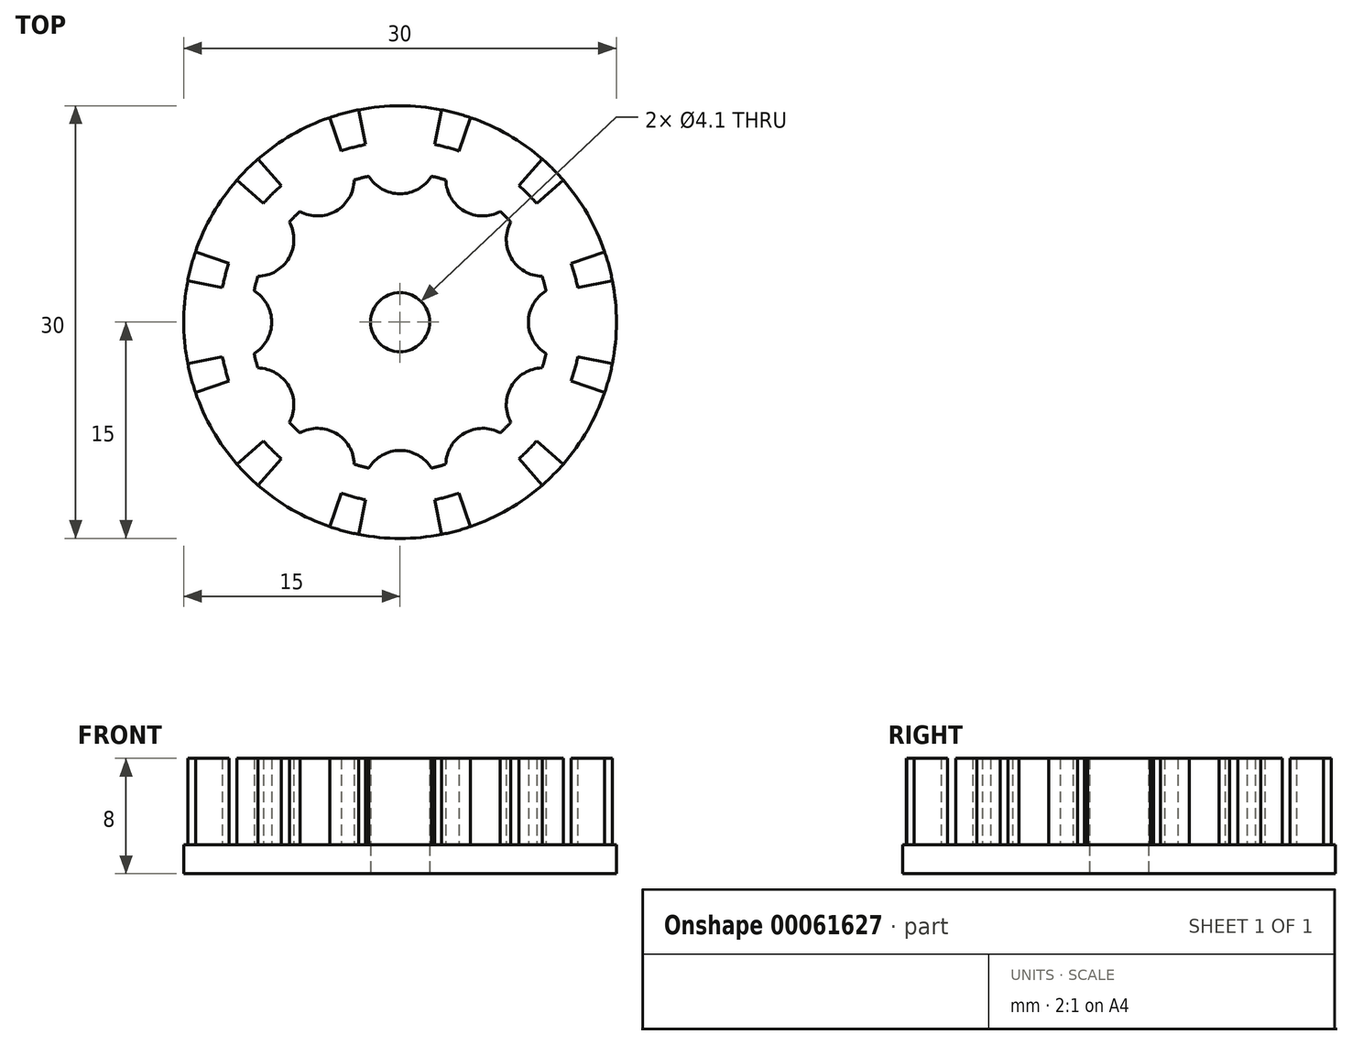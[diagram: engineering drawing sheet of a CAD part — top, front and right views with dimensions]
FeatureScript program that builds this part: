
annotation { "Feature Type Name" : "Feature", "Feature Type Description" : "" }
export const myFeature = defineFeature(function(context is Context, id is Id, definition is map)
    precondition{}
    {
        {
            var Q0;
            Q0=qCreatedBy(makeId("Top.planeOp"),FACE);
            var sketch = newSketch(context, id + "F0", { "sketchPlane" : qUnion([Q0])});
            skCircle(sketch, "E0", {"center": v(0, 0) * mm, "radius": 15 * mm});
            skArc(sketch, "E1.2.0", {"start": v(-9.85, 3.18) * mm, "mid": v(-7.7, 4.45) * mm, "end": v(-7.68, 6.94) * mm});
            skArc(sketch, "E2", {"start": v(-9.85, 3.18) * mm, "mid": v(-10, 2.68) * mm, "end": v(-10.12, 2.18) * mm});
            skArc(sketch, "E3", {"start": v(-11.87, 4.08) * mm, "mid": v(-12.12, 3.25) * mm, "end": v(-12.32, 2.4) * mm});
            skArc(sketch, "E4.trimOffspring", {"start": v(-10.12, -2.18) * mm, "mid": v(-8.9, 0) * mm, "end": v(-10.12, 2.18) * mm});
            skArc(sketch, "E5.trimOffspring", {"start": v(-7.68, -6.94) * mm, "mid": v(-7.7, -4.45) * mm, "end": v(-9.85, -3.18) * mm});
            skArc(sketch, "E6.trimOffspring", {"start": v(-3.18, -9.85) * mm, "mid": v(-4.45, -7.7) * mm, "end": v(-6.94, -7.68) * mm});
            skArc(sketch, "E7.trimOffspring", {"start": v(6.94, -7.68) * mm, "mid": v(4.45, -7.7) * mm, "end": v(3.18, -9.85) * mm});
            skArc(sketch, "E8.trimOffspring", {"start": v(9.85, -3.18) * mm, "mid": v(7.7, -4.45) * mm, "end": v(7.68, -6.94) * mm});
            skArc(sketch, "E9.trimOffspring", {"start": v(10.12, 2.18) * mm, "mid": v(8.9, 0) * mm, "end": v(10.12, -2.18) * mm});
            skArc(sketch, "E10.trimOffspring", {"start": v(7.68, 6.94) * mm, "mid": v(7.7, 4.45) * mm, "end": v(9.85, 3.18) * mm});
            skArc(sketch, "E11.trimOffspring", {"start": v(3.18, 9.85) * mm, "mid": v(4.45, 7.7) * mm, "end": v(6.94, 7.68) * mm});
            skArc(sketch, "E12.trimOffspring", {"start": v(-2.18, 10.12) * mm, "mid": v(0, 8.9) * mm, "end": v(2.18, 10.12) * mm});
            skArc(sketch, "E13.trimOffspring", {"start": v(-6.94, 7.68) * mm, "mid": v(-4.45, 7.7) * mm, "end": v(-3.18, 9.85) * mm});
            skArc(sketch, "E14.trimOffspring", {"start": v(-10.12, -2.18) * mm, "mid": v(-10, -2.68) * mm, "end": v(-9.85, -3.18) * mm});
            skArc(sketch, "E15.trimOffspring", {"start": v(-12.32, -2.4) * mm, "mid": v(-12.12, -3.25) * mm, "end": v(-11.87, -4.08) * mm});
            skArc(sketch, "E16.trimOffspring", {"start": v(-9.47, -8.24) * mm, "mid": v(-8.87, -8.87) * mm, "end": v(-8.24, -9.47) * mm});
            skArc(sketch, "E17.trimOffspring", {"start": v(-7.68, -6.94) * mm, "mid": v(-7.32, -7.32) * mm, "end": v(-6.94, -7.68) * mm});
            skArc(sketch, "E18.trimOffspring", {"start": v(-3.18, -9.85) * mm, "mid": v(-2.68, -10) * mm, "end": v(-2.18, -10.12) * mm});
            skArc(sketch, "E19.trimOffspring", {"start": v(-4.08, -11.87) * mm, "mid": v(-3.25, -12.12) * mm, "end": v(-2.4, -12.32) * mm});
            skArc(sketch, "E20.trimOffspring", {"start": v(2.18, -10.12) * mm, "mid": v(2.68, -10) * mm, "end": v(3.18, -9.85) * mm});
            skArc(sketch, "E21.trimOffspring", {"start": v(2.4, -12.32) * mm, "mid": v(3.25, -12.12) * mm, "end": v(4.08, -11.87) * mm});
            skArc(sketch, "E22.trimOffspring", {"start": v(2.18, -10.12) * mm, "mid": v(0, -8.9) * mm, "end": v(-2.18, -10.12) * mm});
            skArc(sketch, "E23.trimOffspring", {"start": v(8.24, -9.47) * mm, "mid": v(8.87, -8.87) * mm, "end": v(9.47, -8.24) * mm});
            skArc(sketch, "E24.trimOffspring", {"start": v(6.94, -7.68) * mm, "mid": v(7.32, -7.32) * mm, "end": v(7.68, -6.94) * mm});
            skArc(sketch, "E25.trimOffspring", {"start": v(11.87, -4.08) * mm, "mid": v(12.12, -3.25) * mm, "end": v(12.32, -2.4) * mm});
            skArc(sketch, "E26.trimOffspring", {"start": v(9.85, -3.18) * mm, "mid": v(10, -2.68) * mm, "end": v(10.12, -2.18) * mm});
            skArc(sketch, "E27.trimOffspring", {"start": v(12.32, 2.4) * mm, "mid": v(12.12, 3.25) * mm, "end": v(11.87, 4.08) * mm});
            skArc(sketch, "E28.trimOffspring", {"start": v(10.12, 2.18) * mm, "mid": v(10, 2.68) * mm, "end": v(9.85, 3.18) * mm});
            skArc(sketch, "E29.trimOffspring", {"start": v(9.47, 8.24) * mm, "mid": v(8.87, 8.87) * mm, "end": v(8.24, 9.47) * mm});
            skArc(sketch, "E30.trimOffspring", {"start": v(7.68, 6.94) * mm, "mid": v(7.32, 7.32) * mm, "end": v(6.94, 7.68) * mm});
            skArc(sketch, "E31.trimOffspring", {"start": v(3.18, 9.85) * mm, "mid": v(2.68, 10) * mm, "end": v(2.18, 10.12) * mm});
            skArc(sketch, "E32.trimOffspring", {"start": v(4.08, 11.87) * mm, "mid": v(3.25, 12.12) * mm, "end": v(2.4, 12.32) * mm});
            skArc(sketch, "E33.trimOffspring", {"start": v(-2.18, 10.12) * mm, "mid": v(-2.68, 10) * mm, "end": v(-3.18, 9.85) * mm});
            skArc(sketch, "E34.trimOffspring", {"start": v(-2.4, 12.32) * mm, "mid": v(-3.25, 12.12) * mm, "end": v(-4.08, 11.87) * mm});
            skArc(sketch, "E35.trimOffspring", {"start": v(-6.94, 7.68) * mm, "mid": v(-7.32, 7.32) * mm, "end": v(-7.68, 6.94) * mm});
            skArc(sketch, "E36.trimOffspring", {"start": v(-8.24, 9.47) * mm, "mid": v(-8.87, 8.87) * mm, "end": v(-9.47, 8.24) * mm});
            skLineSegment(sketch, "E37", {"start": v(-2.4, -12.32) * mm, "end": v(-2.87, -14.72) * mm});
            skLineSegment(sketch, "E38", {"start": v(-4.08, -11.87) * mm, "end": v(-4.87, -14.19) * mm});
            skLineSegment(sketch, "E39.1.0", {"start": v(4.08, -11.87) * mm, "end": v(4.87, -14.19) * mm});
            skLineSegment(sketch, "E39.1.1", {"start": v(2.4, -12.32) * mm, "end": v(2.88, -14.72) * mm});
            skLineSegment(sketch, "E39.2.0", {"start": v(9.47, -8.24) * mm, "end": v(11.31, -9.85) * mm});
            skLineSegment(sketch, "E39.2.1", {"start": v(8.24, -9.46) * mm, "end": v(9.85, -11.31) * mm});
            skLineSegment(sketch, "E39.3.0", {"start": v(12.32, -2.4) * mm, "end": v(14.72, -2.87) * mm});
            skLineSegment(sketch, "E39.3.1", {"start": v(11.87, -4.08) * mm, "end": v(14.19, -4.87) * mm});
            skLineSegment(sketch, "E39.4.0", {"start": v(11.87, 4.08) * mm, "end": v(14.19, 4.87) * mm});
            skLineSegment(sketch, "E39.4.1", {"start": v(12.32, 2.4) * mm, "end": v(14.72, 2.88) * mm});
            skLineSegment(sketch, "E39.5.0", {"start": v(8.24, 9.47) * mm, "end": v(9.85, 11.31) * mm});
            skLineSegment(sketch, "E39.5.1", {"start": v(9.46, 8.24) * mm, "end": v(11.31, 9.85) * mm});
            skLineSegment(sketch, "E39.6.0", {"start": v(2.4, 12.32) * mm, "end": v(2.87, 14.72) * mm});
            skLineSegment(sketch, "E39.6.1", {"start": v(4.08, 11.87) * mm, "end": v(4.87, 14.19) * mm});
            skLineSegment(sketch, "E39.7.0", {"start": v(-4.08, 11.87) * mm, "end": v(-4.87, 14.19) * mm});
            skLineSegment(sketch, "E39.7.1", {"start": v(-2.4, 12.32) * mm, "end": v(-2.88, 14.72) * mm});
            skLineSegment(sketch, "E39.8.0", {"start": v(-9.47, 8.24) * mm, "end": v(-11.31, 9.85) * mm});
            skLineSegment(sketch, "E39.8.1", {"start": v(-8.24, 9.46) * mm, "end": v(-9.85, 11.31) * mm});
            skLineSegment(sketch, "E39.9.0", {"start": v(-12.32, 2.4) * mm, "end": v(-14.72, 2.87) * mm});
            skLineSegment(sketch, "E39.9.1", {"start": v(-11.87, 4.08) * mm, "end": v(-14.19, 4.87) * mm});
            skLineSegment(sketch, "E39.10.0", {"start": v(-11.87, -4.08) * mm, "end": v(-14.19, -4.87) * mm});
            skLineSegment(sketch, "E39.10.1", {"start": v(-12.32, -2.4) * mm, "end": v(-14.72, -2.88) * mm});
            skLineSegment(sketch, "E39.11.0", {"start": v(-8.24, -9.47) * mm, "end": v(-9.85, -11.31) * mm});
            skLineSegment(sketch, "E39.11.1", {"start": v(-9.46, -8.24) * mm, "end": v(-11.31, -9.85) * mm});
            skSolve(sketch);
        }
        {
            var Q0;
            Q0=makeQuery(id+"F0.imprint","IMPRINT",FACE,{"disambiguationData":[TD([[makeQuery(id+"F0.imprint","IMPRINT",EDGE,{"derivedFrom":sQuery(id+"F0.wireOp",EDGE,"E1.2.0")}),-1.0]])]});
            var Q1;
            {var subQ0=sQuery(id+"F0.wireOp",EDGE,"E39.10.0");Q1=makeQuery(id+"F0.imprint","IMPRINT",FACE,{"disambiguationData":[TD([[makeQuery(id+"F0.imprint","IMPRINT",EDGE,{"derivedFrom":subQ0}),-1.0]])]});}
            var Q2;
            {var subQ0=sQuery(id+"F0.wireOp",EDGE,"E39.9.0");Q2=makeQuery(id+"F0.imprint","IMPRINT",FACE,{"disambiguationData":[TD([[makeQuery(id+"F0.imprint","IMPRINT",EDGE,{"derivedFrom":subQ0}),-1.0]])]});}
            var Q3;
            {var subQ0=sQuery(id+"F0.wireOp",EDGE,"E39.8.0");Q3=makeQuery(id+"F0.imprint","IMPRINT",FACE,{"disambiguationData":[TD([[makeQuery(id+"F0.imprint","IMPRINT",EDGE,{"derivedFrom":subQ0}),-1.0]])]});}
            var Q4;
            {var subQ0=sQuery(id+"F0.wireOp",EDGE,"E39.7.0");Q4=makeQuery(id+"F0.imprint","IMPRINT",FACE,{"disambiguationData":[TD([[makeQuery(id+"F0.imprint","IMPRINT",EDGE,{"derivedFrom":subQ0}),-1.0]])]});}
            var Q5;
            {var subQ0=sQuery(id+"F0.wireOp",EDGE,"E39.6.0");Q5=makeQuery(id+"F0.imprint","IMPRINT",FACE,{"disambiguationData":[TD([[makeQuery(id+"F0.imprint","IMPRINT",EDGE,{"derivedFrom":subQ0}),-1.0]])]});}
            var Q6;
            {var subQ0=sQuery(id+"F0.wireOp",EDGE,"E39.5.0");Q6=makeQuery(id+"F0.imprint","IMPRINT",FACE,{"disambiguationData":[TD([[makeQuery(id+"F0.imprint","IMPRINT",EDGE,{"derivedFrom":subQ0}),-1.0]])]});}
            var Q7;
            {var subQ0=sQuery(id+"F0.wireOp",EDGE,"E39.4.0");Q7=makeQuery(id+"F0.imprint","IMPRINT",FACE,{"disambiguationData":[TD([[makeQuery(id+"F0.imprint","IMPRINT",EDGE,{"derivedFrom":subQ0}),-1.0]])]});}
            var Q8;
            {var subQ0=sQuery(id+"F0.wireOp",EDGE,"E39.3.0");Q8=makeQuery(id+"F0.imprint","IMPRINT",FACE,{"disambiguationData":[TD([[makeQuery(id+"F0.imprint","IMPRINT",EDGE,{"derivedFrom":subQ0}),-1.0]])]});}
            var Q9;
            {var subQ0=sQuery(id+"F0.wireOp",EDGE,"E39.2.0");Q9=makeQuery(id+"F0.imprint","IMPRINT",FACE,{"disambiguationData":[TD([[makeQuery(id+"F0.imprint","IMPRINT",EDGE,{"derivedFrom":subQ0}),-1.0]])]});}
            var Q10;
            {var subQ0=sQuery(id+"F0.wireOp",EDGE,"E39.1.0");Q10=makeQuery(id+"F0.imprint","IMPRINT",FACE,{"disambiguationData":[TD([[makeQuery(id+"F0.imprint","IMPRINT",EDGE,{"derivedFrom":subQ0}),-1.0]])]});}
            var Q11;
            {var subQ0=sQuery(id+"F0.wireOp",EDGE,"E37");Q11=makeQuery(id+"F0.imprint","IMPRINT",FACE,{"disambiguationData":[TD([[makeQuery(id+"F0.imprint","IMPRINT",EDGE,{"derivedFrom":subQ0}),-1.0]])]});}
            var Q12;
            {var subQ0=sQuery(id+"F0.wireOp",EDGE,"E39.11.0");Q12=makeQuery(id+"F0.imprint","IMPRINT",FACE,{"disambiguationData":[TD([[makeQuery(id+"F0.imprint","IMPRINT",EDGE,{"derivedFrom":subQ0}),-1.0]])]});}
            extrude(context, id + "F1", {"entities" : qUnion([Q0, Q1, Q2, Q3, Q4, Q5, Q6, Q7, Q8, Q9, Q10, Q11, Q12]), "depth" : 6 * mm});
        }
        {
            var Q0;
            Q0=makeQuery(id+"F1.opExtrude","CAP_FACE",FACE,{"disambiguationData":[OSD([sQuery(id+"F0.wireOp",EDGE,"E1.2.0"),sQuery(id+"F0.wireOp",EDGE,"E2"),sQuery(id+"F0.wireOp",EDGE,"E4.trimOffspring"),sQuery(id+"F0.wireOp",EDGE,"E5.trimOffspring"),sQuery(id+"F0.wireOp",EDGE,"E6.trimOffspring"),sQuery(id+"F0.wireOp",EDGE,"E7.trimOffspring"),sQuery(id+"F0.wireOp",EDGE,"E8.trimOffspring"),sQuery(id+"F0.wireOp",EDGE,"E9.trimOffspring"),sQuery(id+"F0.wireOp",EDGE,"E10.trimOffspring"),sQuery(id+"F0.wireOp",EDGE,"E11.trimOffspring"),sQuery(id+"F0.wireOp",EDGE,"E12.trimOffspring"),sQuery(id+"F0.wireOp",EDGE,"E13.trimOffspring"),sQuery(id+"F0.wireOp",EDGE,"E14.trimOffspring"),sQuery(id+"F0.wireOp",EDGE,"E17.trimOffspring"),sQuery(id+"F0.wireOp",EDGE,"E18.trimOffspring"),sQuery(id+"F0.wireOp",EDGE,"E20.trimOffspring"),sQuery(id+"F0.wireOp",EDGE,"E22.trimOffspring"),sQuery(id+"F0.wireOp",EDGE,"E24.trimOffspring"),sQuery(id+"F0.wireOp",EDGE,"E26.trimOffspring"),sQuery(id+"F0.wireOp",EDGE,"E28.trimOffspring"),sQuery(id+"F0.wireOp",EDGE,"E30.trimOffspring"),sQuery(id+"F0.wireOp",EDGE,"E31.trimOffspring"),sQuery(id+"F0.wireOp",EDGE,"E33.trimOffspring"),sQuery(id+"F0.wireOp",EDGE,"E35.trimOffspring")])],"isStart":true});
            var sketch = newSketch(context, id + "F2", { "sketchPlane" : qUnion([Q0])});
            skCircle(sketch, "E40", {"center": v(0, 0) * mm, "radius": 15 * mm});
            skSolve(sketch);
        }
        {
            var Q0;
            Q0 = qSketchRegion(id + "F2", true);
            extrude(context, id + "F3", {"entities" : qUnion([Q0]), "depth" : 2 * mm});
        }
        {
            var Q0;
            Q0=makeQuery(id+"F3.opExtrude","CAP_FACE",FACE,{"disambiguationData":[OSD([sQuery(id+"F2.wireOp",EDGE,"E40")])],"isStart":false});
            var sketch = newSketch(context, id + "F4", { "sketchPlane" : qUnion([Q0])});
            skCircle(sketch, "E41", {"center": v(0, 0) * mm, "radius": 2.05 * mm});
            skSolve(sketch);
        }
        {
            var Q0;
            Q0 = qSketchRegion(id + "F4", true);
            extrude(context, id + "F5", {"entities" : qUnion([Q0]), "operationType" : NewBodyOperationType.REMOVE, "endBound" : BoundingType.THROUGH_ALL, "oppositeDirection" : true, "depth" : 25 * mm});
        }
    });
